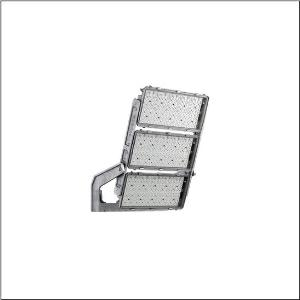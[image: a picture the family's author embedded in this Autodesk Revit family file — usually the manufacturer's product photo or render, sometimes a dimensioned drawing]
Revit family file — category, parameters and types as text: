
# Revit family: floodlight_fl_11_maxi_pro_remote___pl43_5xa779528a01aa_9860
name_source: partatom
category: Lighting Fixtures
units: mm (PartAtom-declared; Revit-internal decimal feet)

## family parameters
Cut with Voids When Loaded = No
Host = Face
Light Source = No
Part Type = Normal
Room Calculation Point = No
Round Connector Dimension = Use Diameter
Shared = No

## types (1)
- --- (1 x LED, 156040 lm, 1388 W, 5700K)
    Apparent Load = 1388 VA
    CIE Flux Codes = 25 74 99 100 100
    Color Rendering = 80
    Color Temperature = 5700K
    Default Elevation = 1800 mm
    Description = Floodlight FL 11  maxi  pro Remote floodlight; light control with lens of PMMA; cover panel of toughened safety glass, transparent; light distribution: PL43, asymmetric direct distribution, LEDcolour temperature: 5700K, rated luminous flux: 156.040lm, colour rendering: CRI > 80, light colour: 857; luminous efficacy: 112lm/W; brightness control: DMX+RDM; with terminal, 8-pole, max. 2.5mm², mains connection: 220..240V/380..400V AC, 50/60Hz, surge voltage resistance: line to ground: 10kV, ECG replaceable separately, LED unit replaceable without ESD environment, dustproof LED module, LED unit replaceable, LED unit replaceable on mast without ESD environment, dimming range 10..100%; 1388W floodlight with 3x LED unit of diecast aluminium, coated grey; length: 1.003mm / width: 651mm / height: 338mm; mounting bracket, of diecast aluminium, uncoated, natural, equipment: Power, protection rating (complete): IP66; insulation class (complete): insulation class I (protective earthing); certification: CE, ENEC, VDE; ball protection: ball impact resistance with accessories, impact resistance: IK07; only for outdoor installations, rated ambient temperature 10°C, permissible operating ambient temperature: -40..+30°C, permissible storage temperature: -40..+85°C; packaging unit: 1 piece

Light Distribution: PL43
    Height = 320 mm
    Lamp = 1 x LED
    Lamp Light Flux = 156040 lm
    Lamp Power = 1388 W
    Lamp count = 1
    Length = 1002 mm
    Luminous efficacy = 112 lm/W
    Manufacturer = Siteco
    ModVariant = No
    Model = 5XA779528A01AA
    Mounting Place = Ceiling
    Mounting Type = Surface mounted
    Number of Poles = 1
    OnlyDefault = Yes
    Power Factor = 1
    Product Name = Floodlight FL 11 maxi pro Remote | PL43
    Product group = floodlight | ceiling mounted
    ProductGroupID = 303
    Protection Class = Protection class I
    Protection Degree = IP 66
    RLX_Detail_Level = 1
    RLX_Emergency_Light_Flux = 0 lm
    RLX_Emergency_Type = 0
    RLX_Emergency_Type_DB = No
    RlxData = <blob elided: 52337 chars, md5=1f85e7c8>
    Socket = socket
    Standby Power = 0 W
    System Light Flux = 156040 lm
    System Power = 1388 W
    Type Comments = factory setting: luminous flux: 100 % | dim-lin: 255 | 955 mA
    Type Image = l_1006784.jpg
    URL = http://relux.com
    VarID = @adj_033381
    Voltage = 0 V
    Weight = 0.00 kg
    Width = 655 mm

## geometry (parser evidence)
native form markers: Blend x4, Sweep x14
no freeform markers — native parametric forms only
